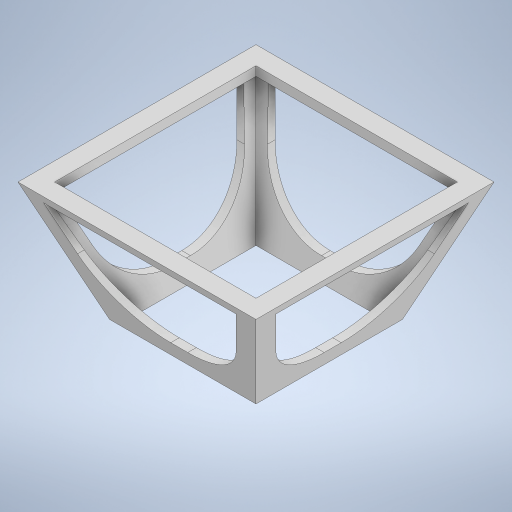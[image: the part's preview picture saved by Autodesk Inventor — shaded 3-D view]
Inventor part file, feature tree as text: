
AUTODESK INVENTOR PART (.ipt)
format: ipt  version: 2023 (Build 270158000, 158)  size: 345,088 bytes
history: native  units: mm
features: sketch x7, plane x4, extrude x3, loft x2, fillet x1
ambient origin geometry x8: Origin, YZ Plane, XZ Plane, XY Plane, X Axis, Y Axis, Z Axis, Center Point
bodies: Solid1 (feature_tree)
feature tree (17):
  sketch  "Sketch1"  dims[d0=80.0mm d1=80.0mm]
  plane  "Work Plane1"
  loft  "Loft1"
  sketch  "Sketch3"  dims[d10=130.0mm d13=130.0mm]
  plane  "Work Plane2"
  loft  "Loft2"
  plane  "Work Plane3"
  extrude  "Extrusion1"  Depth=130.0mm
  plane  "Work Plane4"
  extrude  "Extrusion2"  TaperAngle=0.0deg  [1 undecoded]
  fillet  "Fillet1"  [1 undecoded]
  extrude  "Extrusion3"  Depth=5.0mm
  sketch  "Sketch2"  dims[d6=70.0mm d9=30.0mm]
  sketch  "Sketch4"  dims[d15=30.0mm d16=0.0mm d17=90.0deg d18=0.0mm d19=90.0deg]
  sketch  "Sketch5"  dims[d20=5.0mm d21=5.0mm]
  sketch  "Sketch6"  dims[d22=5.0mm]
  sketch  "Sketch7"  dims[d23=5.0mm d24=-5.0mm d25=5.0mm d26=5.0mm d27=0.0mm d28=90.0deg d29=0.0mm d30=90.0deg d31=35.5mm d32=10.0mm d34=5.0mm d36=10.0mm d37=10.0mm d38=0.0mm d39=0.0mm d40=65.0mm d41=5.0mm d43=10.0mm d44=10.0mm d45=10.0mm d46=10.0mm d47=0.0mm d48=40.0mm d49=10.0mm d50=10.0mm d51=10.0mm d52=10.0mm d53=10.0mm d54=0.0mm]
note: 2 required parameter values undecoded (feature->parameter linkage not recoverable at this tier; creation-order binding heuristic only, values carry confidence <= 0.55)
